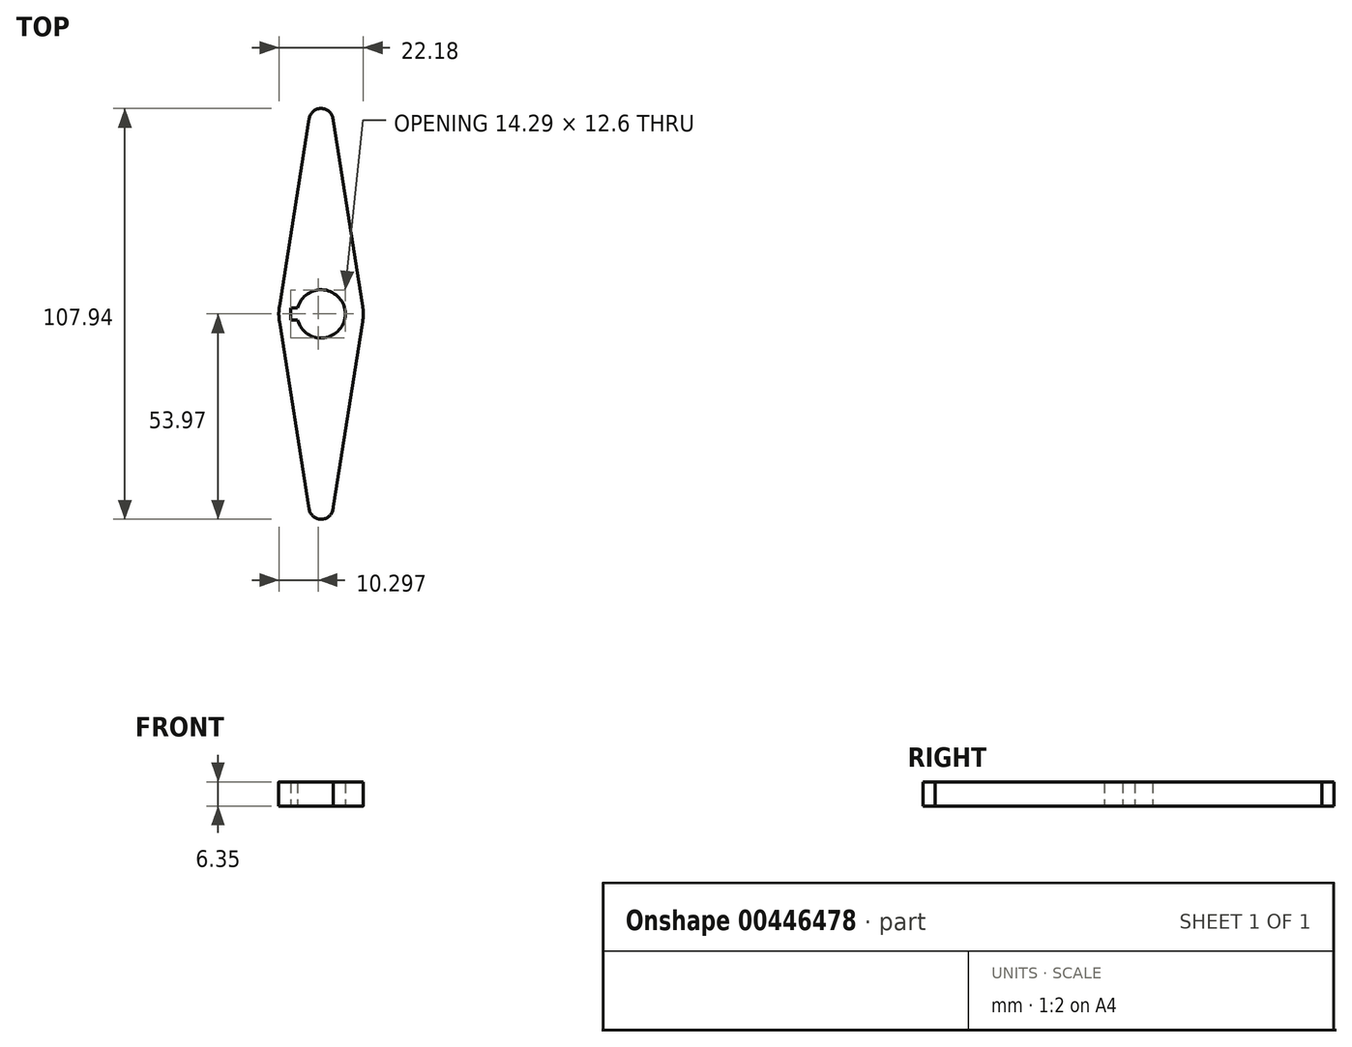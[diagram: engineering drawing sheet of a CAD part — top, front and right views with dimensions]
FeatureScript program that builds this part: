
annotation { "Feature Type Name" : "Feature", "Feature Type Description" : "" }
export const myFeature = defineFeature(function(context is Context, id is Id, definition is map)
    precondition{}
    {
        {
            var Q0;
            Q0=qCreatedBy(makeId("Top.planeOp"),FACE);
            var sketch = newSketch(context, id + "F0", { "sketchPlane" : qUnion([Q0])});
            skCircle(sketch, "E0", {"center": v(0, 0) * mm, "radius": 11.11 * mm});
            skCircle(sketch, "E1", {"center": v(0, 50.8) * mm, "radius": 3.18 * mm});
            skCircle(sketch, "E2", {"center": v(0, -50.8) * mm, "radius": 3.18 * mm});
            skLineSegment(sketch, "E3", {"start": v(-3.14, 51.3) * mm, "end": v(-11.25, 0) * mm});
            skLineSegment(sketch, "E4", {"start": v(-11.25, 0) * mm, "end": v(-3.14, -51.3) * mm});
            skLineSegment(sketch, "E5", {"start": v(3.17, 50.8) * mm, "end": v(11.25, 0) * mm});
            skLineSegment(sketch, "E6", {"start": v(11.25, 0) * mm, "end": v(3.18, -50.8) * mm});
            skArc(sketch, "E7", {"start": v(-6.15, -1.59) * mm, "mid": v(6.35, 0) * mm, "end": v(-6.15, 1.59) * mm});
            skLineSegment(sketch, "E8.bottom", {"start": v(-6.15, 1.59) * mm, "end": v(-7.94, 1.59) * mm});
            skLineSegment(sketch, "E8.top", {"start": v(-6.15, -1.59) * mm, "end": v(-7.94, -1.59) * mm});
            skLineSegment(sketch, "E8.right", {"start": v(-7.94, 1.59) * mm, "end": v(-7.94, -1.59) * mm});
            skPoint(sketch, "E8.middle", {"position": v(-7.04, 0) * mm});
            skSolve(sketch);
        }
        {
            var Q0;
            Q0=qSketchRegion(id+"F0",true);
            extrude(context, id + "F1", {"entities" : qUnion([Q0]), "depth" : 6.35 * mm, "offsetDistance" : 25.4 * mm});
        }
        {
            var Q0;
            Q0=makeQuery(id+"F1.opExtrude","SWEPT_EDGE",EDGE,{"disambiguationData":[OSD([sQuery(id+"F0.wireOp",EDGE,"E3"),sQuery(id+"F0.wireOp",EDGE,"E4")])]});
            var Q1;
            Q1=makeQuery(id+"F1.opExtrude","SWEPT_EDGE",EDGE,{"disambiguationData":[OSD([sQuery(id+"F0.wireOp",EDGE,"E5"),sQuery(id+"F0.wireOp",EDGE,"E6")])]});
            fillet(context, id + "F2", {"entities" : qUnion([Q0, Q1]), "radius" : 12.7 * mm, "tangentPropagation" : true, "allowEdgeOverflow" : false});
        }
    });
